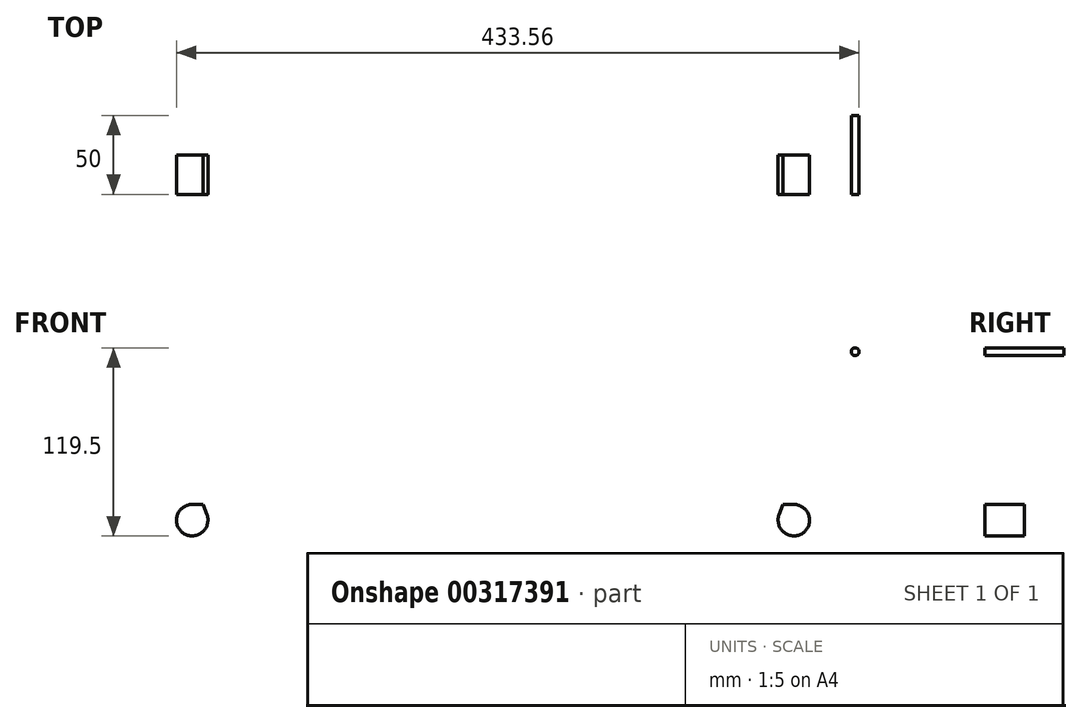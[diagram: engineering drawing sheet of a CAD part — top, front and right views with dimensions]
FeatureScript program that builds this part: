
annotation { "Feature Type Name" : "Feature", "Feature Type Description" : "" }
export const myFeature = defineFeature(function(context is Context, id is Id, definition is map)
    precondition{}
    {
        {
            var Q0;
            Q0=qCreatedBy(makeId("Front.planeOp"),FACE);
            var sketch = newSketch(context, id + "F0", { "sketchPlane" : qUnion([Q0])});
            skLineSegment(sketch, "E0", {"start": v(0, 0) * mm, "end": v(191.06, 0) * mm});
            skLineSegment(sketch, "E1", {"start": v(230, 107) * mm, "end": v(191.06, 0) * mm});
            skArc(sketch, "E2.0.startCap", {"start": v(0, -10) * mm, "mid": v(-10, 0) * mm, "end": v(0, 10) * mm});
            skArc(sketch, "E2.0.endCap", {"start": v(191.06, 10) * mm, "mid": v(201.06, 0) * mm, "end": v(191.06, -10) * mm});
            skLineSegment(sketch, "E2.0.left", {"start": v(0, 10) * mm, "end": v(191.06, 10) * mm});
            skLineSegment(sketch, "E2.0.right", {"start": v(0, -10) * mm, "end": v(191.06, -10) * mm});
            skArc(sketch, "E2.1.startCap", {"start": v(200.45, -3.42) * mm, "mid": v(187.63, -9.4) * mm, "end": v(181.66, 3.42) * mm});
            skArc(sketch, "E2.1.endCap", {"start": v(220.6, 110.42) * mm, "mid": v(233.42, 116.4) * mm, "end": v(239.4, 103.58) * mm});
            skLineSegment(sketch, "E2.1.left", {"start": v(220.6, 110.42) * mm, "end": v(181.66, 3.42) * mm});
            skLineSegment(sketch, "E2.1.right", {"start": v(239.4, 103.58) * mm, "end": v(200.45, -3.42) * mm});
            skCircle(sketch, "E3", {"center": v(230, 107) * mm, "radius": 2.5 * mm});
            skCircle(sketch, "E4", {"center": v(120, 0) * mm, "radius": 2.5 * mm});
            skSolve(sketch);
        }
        {
            var Q0;
            {var subQ4=sQuery(id+"F0.wireOp",EDGE,"E2.0.startCap");Q0=makeQuery(id+"F0.imprint","IMPRINT",FACE,{"disambiguationData":[TD([[makeQuery(id+"F0.imprint","IMPRINT",EDGE,{"derivedFrom":subQ4}),-1.0]])]});}
            var Q1;
            {var subQ4=sQuery(id+"F0.wireOp",EDGE,"E1");var subQ6=sQuery(id+"F0.wireOp",EDGE,"E0");var subQ7=makeQuery(id+"F0.imprint","INTERSECT",VERTEX,{"derivedFrom":[subQ6,subQ4]});Q1=makeQuery(id+"F0.imprint","IMPRINT",FACE,{"disambiguationData":[TD([[makeQuery(id+"F0.imprint","IMPRINT",EDGE,{"disambiguationData":[TD([[subQ7,1.0]])],"derivedFrom":subQ6}),-1.0]])]});}
            var Q2;
            {var subQ0=sQuery(id+"F0.wireOp",EDGE,"E2.1.endCap");Q2=makeQuery(id+"F0.imprint","IMPRINT",FACE,{"disambiguationData":[TD([[makeQuery(id+"F0.imprint","IMPRINT",EDGE,{"derivedFrom":subQ0}),-1.0]])]});}
            var Q3;
            {var subQ3=sQuery(id+"F0.wireOp",EDGE,"E1");var subQ7=sQuery(id+"F0.wireOp",EDGE,"E0");var subQ8=makeQuery(id+"F0.imprint","INTERSECT",VERTEX,{"derivedFrom":[subQ7,subQ3]});Q3=makeQuery(id+"F0.imprint","IMPRINT",FACE,{"disambiguationData":[TD([[makeQuery(id+"F0.imprint","IMPRINT",EDGE,{"disambiguationData":[TD([[subQ8,1.0]])],"derivedFrom":subQ7}),1.0]])]});}
            var Q4;
            Q4=makeQuery(id+"F0.imprint","IMPRINT",FACE,{"disambiguationData":[TD([[makeQuery(id+"F0.imprint","IMPRINT",EDGE,{"derivedFrom":sQuery(id+"F0.wireOp",EDGE,"E3")}),1.0]])]});
            var Q5;
            {var subQ0=sQuery(id+"F0.wireOp",EDGE,"E4");var subQ1=sQuery(id+"F0.wireOp",EDGE,"E0");var subQ2=makeQuery(id+"F0.imprint","INTERSECT",VERTEX,{"disambiguationData":[OD(0.0)],"derivedFrom":[subQ1,subQ0]});Q5=makeQuery(id+"F0.imprint","IMPRINT",FACE,{"disambiguationData":[TD([[makeQuery(id+"F0.imprint","IMPRINT",EDGE,{"disambiguationData":[TD([[subQ2,-1.0]])],"derivedFrom":subQ1}),-1.0]])]});}
            var Q6;
            {var subQ0=sQuery(id+"F0.wireOp",EDGE,"E4");var subQ1=sQuery(id+"F0.wireOp",EDGE,"E0");var subQ2=makeQuery(id+"F0.imprint","INTERSECT",VERTEX,{"disambiguationData":[OD(0.0)],"derivedFrom":[subQ1,subQ0]});Q6=makeQuery(id+"F0.imprint","IMPRINT",FACE,{"disambiguationData":[TD([[makeQuery(id+"F0.imprint","IMPRINT",EDGE,{"disambiguationData":[TD([[subQ2,-1.0]])],"derivedFrom":subQ1}),1.0]])]});}
            extrude(context, id + "F1", {"entities" : qUnion([Q0, Q1, Q2, Q3, Q4, Q5, Q6]), "depth" : 50 * mm});
        }
        {
            var Q0;
            Q0 = qSketchRegion(id + "F0", true);
            var Q1;
            Q1=sQuery(id+"F0.wireOp",EDGE,"E4");
            var Q2;
            Q2=sQuery(id+"F0.wireOp",EDGE,"E3");
            extrude(context, id + "F2", {"entities" : qUnion([Q0]), "operationType" : NewBodyOperationType.REMOVE, "surfaceEntities" : qUnion([Q1, Q2]), "depth" : 25 * mm});
        }
        {
            var Q0;
            Q0=makeQuery(id+"F1.opExtrude","SWEPT_BODY",BODY,{"disambiguationData":[OSD([sQuery(id+"F0.wireOp",EDGE,"E2.0.startCap"),sQuery(id+"F0.wireOp",EDGE,"E2.0.left"),sQuery(id+"F0.wireOp",EDGE,"E2.0.right"),sQuery(id+"F0.wireOp",EDGE,"E2.1.startCap"),sQuery(id+"F0.wireOp",EDGE,"E2.1.endCap"),sQuery(id+"F0.wireOp",EDGE,"E2.1.left"),sQuery(id+"F0.wireOp",EDGE,"E2.1.right")])]});
            var Q1;
            Q1=qCreatedBy(makeId("Right.planeOp"),FACE);
            mirror(context, id + "F3", {"operationType" : NewBodyOperationType.ADD, "entities" : qUnion([Q0]), "mirrorPlane" : qUnion([Q1])});
        }
        {
            var Q0;
            Q0=makeQuery(id+"F1.opExtrude","SWEPT_BODY",BODY,{"disambiguationData":[OSD([sQuery(id+"F0.wireOp",EDGE,"E2.0.startCap"),sQuery(id+"F0.wireOp",EDGE,"E2.0.left"),sQuery(id+"F0.wireOp",EDGE,"E2.0.right"),sQuery(id+"F0.wireOp",EDGE,"E2.1.startCap"),sQuery(id+"F0.wireOp",EDGE,"E2.1.endCap"),sQuery(id+"F0.wireOp",EDGE,"E2.1.left"),sQuery(id+"F0.wireOp",EDGE,"E2.1.right")])]});
            transform(context, id + "F4", {"entities" : qUnion([Q0]), "transformType" : TransformType.TRANSLATION_3D, "dx" : 0 * mm, "dy" : 0 * mm, "dz" : 0 * mm, "makeCopy" : true});
        }
        {
            var Q0;
            Q0=makeQuery(id+"F4.opPattern","COPY",BODY,{"derivedFrom":makeQuery(id+"F1.opExtrude","SWEPT_BODY",BODY,{"disambiguationData":[OSD([sQuery(id+"F0.wireOp",EDGE,"E2.0.startCap"),sQuery(id+"F0.wireOp",EDGE,"E2.0.left"),sQuery(id+"F0.wireOp",EDGE,"E2.0.right"),sQuery(id+"F0.wireOp",EDGE,"E2.1.startCap"),sQuery(id+"F0.wireOp",EDGE,"E2.1.endCap"),sQuery(id+"F0.wireOp",EDGE,"E2.1.left"),sQuery(id+"F0.wireOp",EDGE,"E2.1.right")])]}),"instanceName":"1"});
            deleteBodies(context, id + "F5", {"entities" : qUnion([Q0])});
        }
    });
